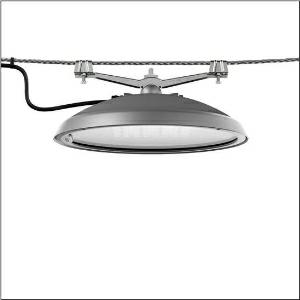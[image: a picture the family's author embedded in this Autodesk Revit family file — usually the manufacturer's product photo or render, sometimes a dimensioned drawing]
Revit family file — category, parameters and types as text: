
# Revit family: dl_r__50_iq_mini___st0_8s_5xa248v31f08fe_ae35
name_source: partatom
category: Lighting Fixtures
units: mm (PartAtom-declared; Revit-internal decimal feet)

## family parameters
Cut with Voids When Loaded = No
Host = Face
Light Source = No
Part Type = Normal
Room Calculation Point = No
Round Connector Dimension = Use Diameter
Shared = No

## types (1)
- --- (1 x LED, 2700 lm, 16.3 W, 3000K)
    Apparent Load = 16 VA
    CIE Flux Codes = 38 75 97 100 100
    Color Rendering = 70
    Color Temperature = 3000K
    Default Elevation = 1800 mm
    Description = DL® 50 iQ mini, catenary luminaire, primary light control with lens, of PMMA, primary optical cover: cover, of toughened safety glass, transparent, light distribution: ST0.8s, light emission: direct distribution, primary light characteristic: symmetric, installation type: suspended mounting, LED, High Power LED, rated luminous flux: 2.700lm, luminous efficacy: 166lm/W, light colour: 730, colour temperature: 3000K, control gear: iQ Street-Remote, control: optimised constant luminous flux control (CLO 2.0), Desk-Remote (wireless, voltage-free reading and setting of iQ features in the workshop via application-optimized NFC function/RFID function), Light-Fading, Smart-Wire, Night-Set, Lumen-Switch, Temp-Guard, Auto-Match, Street-Remote, mains connection: 230..240V, AC, 50/60Hz, start of lifetime: 16W, end of service life: 17W, reduction: 8W, luminaire housing, of diecast aluminium, powder-coated, Siteco® metallic grey (DB 702S), diameter: 500mm, height: 115mm, mounting height: 4..12m, protection rating (complete): IP66, insulation class (complete): insulation class II (safety insulation), certification: CE, ENEC, ENEC+, VDE, impact resistance: IK08, permissible operating ambient temperature for outdoor applications: -25..+40°C, standard-compliant lighting for roads and squares, packaging unit: 1 piece

Light Distribution: ST0.8s
    Height = 124 mm  [stored 0.406824 ft]
    Lamp = 1 x LED
    Lamp Light Flux = 2700 lm
    Lamp Power = 16.3 W
    Lamp count = 1
    Length = 500 mm
    Luminous efficacy = 166 lm/W
    Manufacturer = Siteco
    ModVariant = No
    Model = 5XA248V31F08FE
    Number of Poles = 1
    OnlyDefault = Yes
    Power Factor = 1
    Product Name = DL® 50 iQ mini | ST0.8s
    Product group = catenary luminaire
    ProductGroupID = 6300
    Protection Class = Protection class II
    Protection Degree = IP 66
    RLX_Detail_Level = 1
    RLX_Emergency_Light_Flux = 0 lm
    RLX_Emergency_Type = 0
    RLX_Emergency_Type_DB = No
    RlxData = <blob elided: 123065 chars, md5=169b5786>
    Socket = socket
    Standby Power = 0 W
    System Light Flux = 2700 lm
    System Power = 16 W
    Type Comments = factory setting: luminous flux: 100 % | dim-lin: 254 | 333 mA
    Type Image = l_1242791.jpg
    URL = http://relux.com
    VarID = @adj_159445
    Voltage = 0 V
    Weight = 0.00 kg
    Width = 0 mm  [stored 0 ft]

note: [stored X ft] marks values corroborated as IEEE doubles in the binary element streams (Revit-internal decimal feet)

## geometry (parser evidence)
native form markers: Blend x4, Sweep x14
no freeform markers — native parametric forms only
